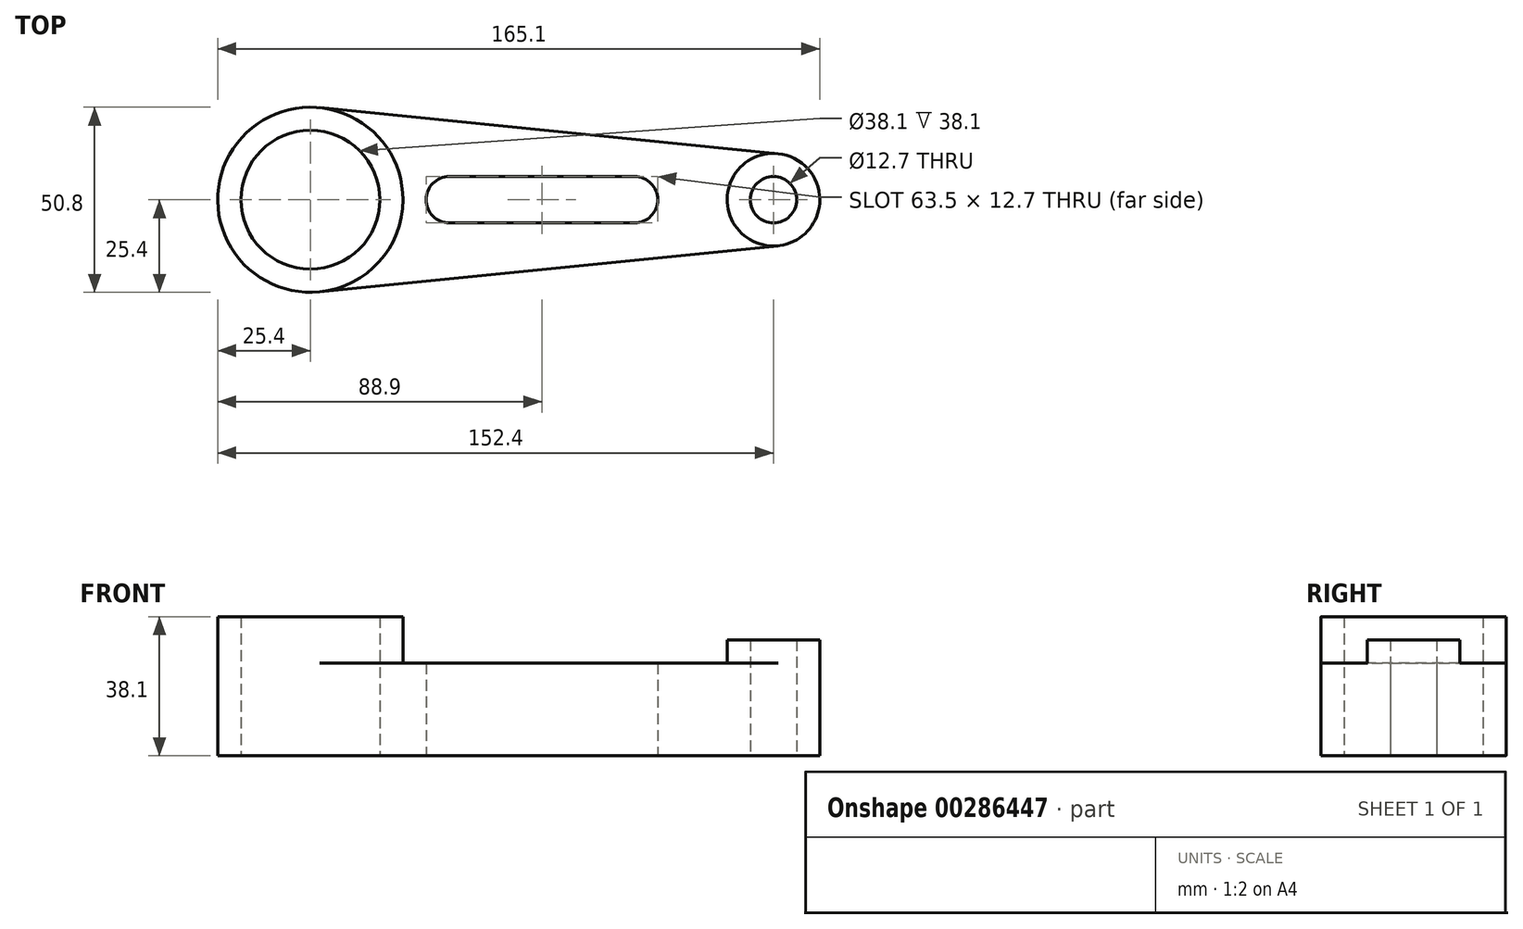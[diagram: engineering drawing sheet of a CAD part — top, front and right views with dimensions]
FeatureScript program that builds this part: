
annotation { "Feature Type Name" : "Feature", "Feature Type Description" : "" }
export const myFeature = defineFeature(function(context is Context, id is Id, definition is map)
    precondition{}
    {
        {
            var Q0;
            Q0=qCreatedBy(makeId("Top.planeOp"),FACE);
            var sketch = newSketch(context, id + "F0", { "sketchPlane" : qUnion([Q0])});
            skCircle(sketch, "E0", {"center": v(88.9, 0) * mm, "radius": 6.35 * mm});
            skCircle(sketch, "E1", {"center": v(88.9, 0) * mm, "radius": 12.7 * mm});
            skCircle(sketch, "E2", {"center": v(-38.1, 0) * mm, "radius": 19.05 * mm});
            skCircle(sketch, "E3", {"center": v(-38.1, 0) * mm, "radius": 25.4 * mm});
            skLineSegment(sketch, "E4", {"start": v(90.17, 12.64) * mm, "end": v(-35.56, 25.27) * mm});
            skLineSegment(sketch, "E5.MirrorCS", {"start": v(90.17, -12.64) * mm, "end": v(-35.56, -25.27) * mm});
            skLineSegment(sketch, "E6", {"start": v(0, 6.35) * mm, "end": v(50.8, 6.35) * mm});
            skLineSegment(sketch, "E7.MirrorCS", {"start": v(0, -6.35) * mm, "end": v(50.8, -6.35) * mm});
            skArc(sketch, "E8", {"start": v(50.8, -6.35) * mm, "mid": v(57.15, 0) * mm, "end": v(50.8, 6.35) * mm});
            skArc(sketch, "E9", {"start": v(0, 6.35) * mm, "mid": v(-6.35, 0) * mm, "end": v(0, -6.35) * mm});
            skSolve(sketch);
        }
        {
            var Q0;
            Q0=makeQuery(id+"F0.imprint","IMPRINT",FACE,{"disambiguationData":[TD([[makeQuery(id+"F0.imprint","IMPRINT",EDGE,{"derivedFrom":sQuery(id+"F0.wireOp",EDGE,"E2")}),-1.0]])]});
            extrude(context, id + "F1", {"entities" : qUnion([Q0]), "depth" : 38.1 * mm});
        }
        {
            var Q0;
            {var subQ1=sQuery(id+"F0.wireOp",EDGE,"E4");Q0=makeQuery(id+"F0.imprint","IMPRINT",FACE,{"disambiguationData":[TD([[makeQuery(id+"F0.imprint","IMPRINT",EDGE,{"derivedFrom":subQ1}),1.0]])]});}
            extrude(context, id + "F2", {"entities" : qUnion([Q0]), "operationType" : NewBodyOperationType.ADD, "depth" : 25.4 * mm});
        }
        {
            var Q0;
            Q0=makeQuery(id+"F0.imprint","IMPRINT",FACE,{"disambiguationData":[TD([[makeQuery(id+"F0.imprint","IMPRINT",EDGE,{"derivedFrom":sQuery(id+"F0.wireOp",EDGE,"E0")}),-1.0]])]});
            extrude(context, id + "F3", {"entities" : qUnion([Q0]), "operationType" : NewBodyOperationType.ADD, "depth" : 31.75 * mm});
        }
    });
